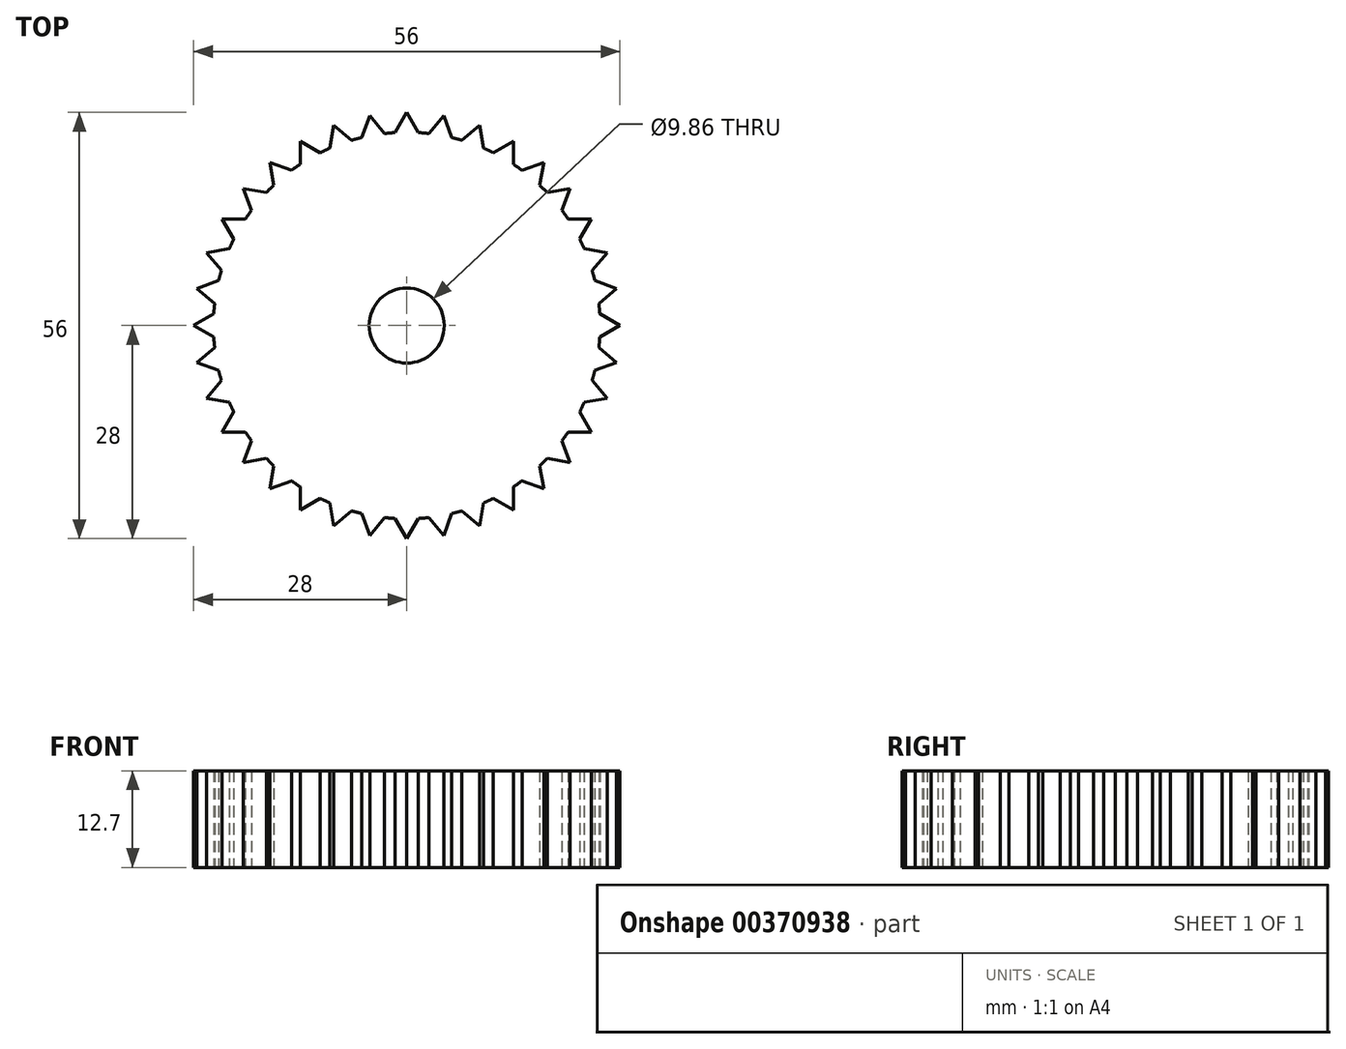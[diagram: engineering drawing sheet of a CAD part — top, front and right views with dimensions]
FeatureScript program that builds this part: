
annotation { "Feature Type Name" : "Feature", "Feature Type Description" : "" }
export const myFeature = defineFeature(function(context is Context, id is Id, definition is map)
    precondition{}
    {
        {
            var Q0;
            Q0=qCreatedBy(makeId("Top.planeOp"),FACE);
            var sketch = newSketch(context, id + "F0", { "sketchPlane" : qUnion([Q0])});
            skCircle(sketch, "E0", {"center": v(0, 0) * mm, "radius": 25.4 * mm});
            skCircle(sketch, "E1", {"center": v(0, 0) * mm, "radius": 4.93 * mm});
            skLineSegment(sketch, "E2", {"start": v(0, 28) * mm, "end": v(1.52, 25.35) * mm});
            skLineSegment(sketch, "E3", {"start": v(0, 28) * mm, "end": v(-1.52, 25.35) * mm});
            skLineSegment(sketch, "E4.1.0", {"start": v(-4.86, 27.57) * mm, "end": v(-2.9, 25.23) * mm});
            skLineSegment(sketch, "E4.1.1", {"start": v(-4.86, 27.57) * mm, "end": v(-5.9, 24.7) * mm});
            skLineSegment(sketch, "E4.2.0", {"start": v(-9.58, 26.3) * mm, "end": v(-7.24, 24.34) * mm});
            skLineSegment(sketch, "E4.2.1", {"start": v(-9.58, 26.3) * mm, "end": v(-10.1, 23.3) * mm});
            skLineSegment(sketch, "E5.3.3.0", {"start": v(-14, 24.25) * mm, "end": v(-14, 21.2) * mm});
            skLineSegment(sketch, "E5.5.3.0", {"start": v(-14, 24.25) * mm, "end": v(-11.36, 22.72) * mm});
            skLineSegment(sketch, "E5.3.4.0", {"start": v(-18, 21.45) * mm, "end": v(-17.46, 18.45) * mm});
            skLineSegment(sketch, "E5.5.4.0", {"start": v(-18, 21.45) * mm, "end": v(-15.13, 20.4) * mm});
            skLineSegment(sketch, "E5.3.5.0", {"start": v(-21.45, 18) * mm, "end": v(-20.4, 15.13) * mm});
            skLineSegment(sketch, "E5.5.5.0", {"start": v(-21.45, 18) * mm, "end": v(-18.45, 17.46) * mm});
            skLineSegment(sketch, "E6.3.6.0", {"start": v(-24.25, 14) * mm, "end": v(-22.72, 11.36) * mm});
            skLineSegment(sketch, "E6.5.6.0", {"start": v(-24.25, 14) * mm, "end": v(-21.2, 14) * mm});
            skLineSegment(sketch, "E6.3.7.0", {"start": v(-26.3, 9.58) * mm, "end": v(-24.34, 7.24) * mm});
            skLineSegment(sketch, "E6.5.7.0", {"start": v(-26.3, 9.58) * mm, "end": v(-23.3, 10.1) * mm});
            skLineSegment(sketch, "E6.3.8.0", {"start": v(-27.57, 4.86) * mm, "end": v(-25.23, 2.9) * mm});
            skLineSegment(sketch, "E6.5.8.0", {"start": v(-27.57, 4.86) * mm, "end": v(-24.7, 5.9) * mm});
            skLineSegment(sketch, "E6.3.9.0", {"start": v(-28, 0) * mm, "end": v(-25.35, -1.52) * mm});
            skLineSegment(sketch, "E6.5.9.0", {"start": v(-28, 0) * mm, "end": v(-25.35, 1.52) * mm});
            skLineSegment(sketch, "E6.3.10.0", {"start": v(-27.57, -4.86) * mm, "end": v(-24.7, -5.9) * mm});
            skLineSegment(sketch, "E6.5.10.0", {"start": v(-27.57, -4.86) * mm, "end": v(-25.23, -2.9) * mm});
            skLineSegment(sketch, "E6.3.11.0", {"start": v(-26.3, -9.58) * mm, "end": v(-23.3, -10.1) * mm});
            skLineSegment(sketch, "E6.5.11.0", {"start": v(-26.3, -9.58) * mm, "end": v(-24.34, -7.24) * mm});
            skLineSegment(sketch, "E6.3.12.0", {"start": v(-24.25, -14) * mm, "end": v(-21.2, -14) * mm});
            skLineSegment(sketch, "E6.5.12.0", {"start": v(-24.25, -14) * mm, "end": v(-22.72, -11.36) * mm});
            skLineSegment(sketch, "E6.3.13.0", {"start": v(-21.45, -18) * mm, "end": v(-18.45, -17.46) * mm});
            skLineSegment(sketch, "E6.5.13.0", {"start": v(-21.45, -18) * mm, "end": v(-20.4, -15.13) * mm});
            skLineSegment(sketch, "E6.3.14.0", {"start": v(-18, -21.45) * mm, "end": v(-15.13, -20.4) * mm});
            skLineSegment(sketch, "E6.5.14.0", {"start": v(-18, -21.45) * mm, "end": v(-17.46, -18.45) * mm});
            skLineSegment(sketch, "E6.3.15.0", {"start": v(-14, -24.25) * mm, "end": v(-11.36, -22.72) * mm});
            skLineSegment(sketch, "E6.5.15.0", {"start": v(-14, -24.25) * mm, "end": v(-14, -21.2) * mm});
            skLineSegment(sketch, "E6.3.16.0", {"start": v(-9.58, -26.3) * mm, "end": v(-7.24, -24.34) * mm});
            skLineSegment(sketch, "E6.5.16.0", {"start": v(-9.58, -26.3) * mm, "end": v(-10.1, -23.3) * mm});
            skLineSegment(sketch, "E6.3.17.0", {"start": v(-4.86, -27.57) * mm, "end": v(-2.9, -25.23) * mm});
            skLineSegment(sketch, "E6.5.17.0", {"start": v(-4.86, -27.57) * mm, "end": v(-5.9, -24.7) * mm});
            skLineSegment(sketch, "E6.3.18.0", {"start": v(0, -28) * mm, "end": v(1.52, -25.35) * mm});
            skLineSegment(sketch, "E6.5.18.0", {"start": v(0, -28) * mm, "end": v(-1.52, -25.35) * mm});
            skLineSegment(sketch, "E6.3.19.0", {"start": v(4.86, -27.57) * mm, "end": v(5.9, -24.7) * mm});
            skLineSegment(sketch, "E6.5.19.0", {"start": v(4.86, -27.57) * mm, "end": v(2.9, -25.23) * mm});
            skLineSegment(sketch, "E6.3.20.0", {"start": v(9.58, -26.3) * mm, "end": v(10.1, -23.3) * mm});
            skLineSegment(sketch, "E6.5.20.0", {"start": v(9.58, -26.3) * mm, "end": v(7.24, -24.34) * mm});
            skLineSegment(sketch, "E6.3.21.0", {"start": v(14, -24.25) * mm, "end": v(14, -21.2) * mm});
            skLineSegment(sketch, "E6.5.21.0", {"start": v(14, -24.25) * mm, "end": v(11.36, -22.72) * mm});
            skLineSegment(sketch, "E6.3.22.0", {"start": v(18, -21.45) * mm, "end": v(17.46, -18.45) * mm});
            skLineSegment(sketch, "E6.5.22.0", {"start": v(18, -21.45) * mm, "end": v(15.13, -20.4) * mm});
            skLineSegment(sketch, "E6.3.23.0", {"start": v(21.45, -18) * mm, "end": v(20.4, -15.13) * mm});
            skLineSegment(sketch, "E6.5.23.0", {"start": v(21.45, -18) * mm, "end": v(18.45, -17.46) * mm});
            skLineSegment(sketch, "E6.3.24.0", {"start": v(24.25, -14) * mm, "end": v(22.72, -11.36) * mm});
            skLineSegment(sketch, "E6.5.24.0", {"start": v(24.25, -14) * mm, "end": v(21.2, -14) * mm});
            skLineSegment(sketch, "E6.3.25.0", {"start": v(26.3, -9.58) * mm, "end": v(24.34, -7.24) * mm});
            skLineSegment(sketch, "E6.5.25.0", {"start": v(26.3, -9.58) * mm, "end": v(23.3, -10.1) * mm});
            skLineSegment(sketch, "E6.3.26.0", {"start": v(27.57, -4.86) * mm, "end": v(25.23, -2.9) * mm});
            skLineSegment(sketch, "E6.5.26.0", {"start": v(27.57, -4.86) * mm, "end": v(24.7, -5.9) * mm});
            skLineSegment(sketch, "E6.3.27.0", {"start": v(28, 0) * mm, "end": v(25.35, 1.52) * mm});
            skLineSegment(sketch, "E6.5.27.0", {"start": v(28, 0) * mm, "end": v(25.35, -1.52) * mm});
            skLineSegment(sketch, "E7.3.28.0", {"start": v(27.57, 4.86) * mm, "end": v(24.7, 5.9) * mm});
            skLineSegment(sketch, "E7.5.28.0", {"start": v(27.57, 4.86) * mm, "end": v(25.23, 2.9) * mm});
            skLineSegment(sketch, "E7.3.29.0", {"start": v(26.3, 9.58) * mm, "end": v(23.3, 10.1) * mm});
            skLineSegment(sketch, "E7.5.29.0", {"start": v(26.3, 9.58) * mm, "end": v(24.34, 7.24) * mm});
            skLineSegment(sketch, "E7.3.30.0", {"start": v(24.25, 14) * mm, "end": v(21.2, 14) * mm});
            skLineSegment(sketch, "E7.5.30.0", {"start": v(24.25, 14) * mm, "end": v(22.72, 11.36) * mm});
            skLineSegment(sketch, "E7.3.31.0", {"start": v(21.45, 18) * mm, "end": v(18.45, 17.46) * mm});
            skLineSegment(sketch, "E7.5.31.0", {"start": v(21.45, 18) * mm, "end": v(20.4, 15.13) * mm});
            skLineSegment(sketch, "E7.3.32.0", {"start": v(18, 21.45) * mm, "end": v(15.13, 20.4) * mm});
            skLineSegment(sketch, "E7.5.32.0", {"start": v(18, 21.45) * mm, "end": v(17.46, 18.45) * mm});
            skLineSegment(sketch, "E7.3.33.0", {"start": v(14, 24.25) * mm, "end": v(11.36, 22.72) * mm});
            skLineSegment(sketch, "E7.5.33.0", {"start": v(14, 24.25) * mm, "end": v(14, 21.2) * mm});
            skLineSegment(sketch, "E7.3.34.0", {"start": v(9.58, 26.3) * mm, "end": v(7.24, 24.34) * mm});
            skLineSegment(sketch, "E7.5.34.0", {"start": v(9.58, 26.3) * mm, "end": v(10.1, 23.3) * mm});
            skLineSegment(sketch, "E7.3.35.0", {"start": v(4.86, 27.57) * mm, "end": v(2.9, 25.23) * mm});
            skLineSegment(sketch, "E7.5.35.0", {"start": v(4.86, 27.57) * mm, "end": v(5.9, 24.7) * mm});
            skSolve(sketch);
        }
        {
            var Q0;
            Q0 = qSketchRegion(id + "F0", true);
            var Q1;
            {var subQ0=sQuery(id+"F0.wireOp",EDGE,"E6.3.14.0");Q1=makeQuery(id+"F0.imprint","IMPRINT",FACE,{"disambiguationData":[TD([[makeQuery(id+"F0.imprint","IMPRINT",EDGE,{"derivedFrom":subQ0}),1.0]])]});}
            var Q2;
            {var subQ0=sQuery(id+"F0.wireOp",EDGE,"E6.3.17.0");Q2=makeQuery(id+"F0.imprint","IMPRINT",FACE,{"disambiguationData":[TD([[makeQuery(id+"F0.imprint","IMPRINT",EDGE,{"derivedFrom":subQ0}),1.0]])]});}
            var Q3;
            {var subQ0=sQuery(id+"F0.wireOp",EDGE,"E6.3.26.0");Q3=makeQuery(id+"F0.imprint","IMPRINT",FACE,{"disambiguationData":[TD([[makeQuery(id+"F0.imprint","IMPRINT",EDGE,{"derivedFrom":subQ0}),1.0]])]});}
            var Q4;
            {var subQ0=sQuery(id+"F0.wireOp",EDGE,"E6.3.25.0");Q4=makeQuery(id+"F0.imprint","IMPRINT",FACE,{"disambiguationData":[TD([[makeQuery(id+"F0.imprint","IMPRINT",EDGE,{"derivedFrom":subQ0}),1.0]])]});}
            var Q5;
            {var subQ0=sQuery(id+"F0.wireOp",EDGE,"E4.2.0");Q5=makeQuery(id+"F0.imprint","IMPRINT",FACE,{"disambiguationData":[TD([[makeQuery(id+"F0.imprint","IMPRINT",EDGE,{"derivedFrom":subQ0}),-1.0]])]});}
            var Q6;
            {var subQ0=sQuery(id+"F0.wireOp",EDGE,"E4.1.0");Q6=makeQuery(id+"F0.imprint","IMPRINT",FACE,{"disambiguationData":[TD([[makeQuery(id+"F0.imprint","IMPRINT",EDGE,{"derivedFrom":subQ0}),-1.0]])]});}
            var Q7;
            {var subQ0=sQuery(id+"F0.wireOp",EDGE,"E7.3.34.0");Q7=makeQuery(id+"F0.imprint","IMPRINT",FACE,{"disambiguationData":[TD([[makeQuery(id+"F0.imprint","IMPRINT",EDGE,{"derivedFrom":subQ0}),1.0]])]});}
            var Q8;
            {var subQ0=sQuery(id+"F0.wireOp",EDGE,"E7.3.29.0");Q8=makeQuery(id+"F0.imprint","IMPRINT",FACE,{"disambiguationData":[TD([[makeQuery(id+"F0.imprint","IMPRINT",EDGE,{"derivedFrom":subQ0}),1.0]])]});}
            var Q9;
            {var subQ0=sQuery(id+"F0.wireOp",EDGE,"E6.3.8.0");Q9=makeQuery(id+"F0.imprint","IMPRINT",FACE,{"disambiguationData":[TD([[makeQuery(id+"F0.imprint","IMPRINT",EDGE,{"derivedFrom":subQ0}),1.0]])]});}
            var Q10;
            {var subQ0=sQuery(id+"F0.wireOp",EDGE,"E5.3.5.0");Q10=makeQuery(id+"F0.imprint","IMPRINT",FACE,{"disambiguationData":[TD([[makeQuery(id+"F0.imprint","IMPRINT",EDGE,{"derivedFrom":subQ0}),1.0]])]});}
            var Q11;
            {var subQ0=sQuery(id+"F0.wireOp",EDGE,"E6.3.18.0");Q11=makeQuery(id+"F0.imprint","IMPRINT",FACE,{"disambiguationData":[TD([[makeQuery(id+"F0.imprint","IMPRINT",EDGE,{"derivedFrom":subQ0}),1.0]])]});}
            var Q12;
            {var subQ0=sQuery(id+"F0.wireOp",EDGE,"E6.3.10.0");Q12=makeQuery(id+"F0.imprint","IMPRINT",FACE,{"disambiguationData":[TD([[makeQuery(id+"F0.imprint","IMPRINT",EDGE,{"derivedFrom":subQ0}),1.0]])]});}
            var Q13;
            {var subQ0=sQuery(id+"F0.wireOp",EDGE,"E5.3.4.0");Q13=makeQuery(id+"F0.imprint","IMPRINT",FACE,{"disambiguationData":[TD([[makeQuery(id+"F0.imprint","IMPRINT",EDGE,{"derivedFrom":subQ0}),1.0]])]});}
            var Q14;
            {var subQ0=sQuery(id+"F0.wireOp",EDGE,"E2");Q14=makeQuery(id+"F0.imprint","IMPRINT",FACE,{"disambiguationData":[TD([[makeQuery(id+"F0.imprint","IMPRINT",EDGE,{"derivedFrom":subQ0}),-1.0]])]});}
            var Q15;
            {var subQ0=sQuery(id+"F0.wireOp",EDGE,"E7.3.30.0");Q15=makeQuery(id+"F0.imprint","IMPRINT",FACE,{"disambiguationData":[TD([[makeQuery(id+"F0.imprint","IMPRINT",EDGE,{"derivedFrom":subQ0}),1.0]])]});}
            var Q16;
            {var subQ0=sQuery(id+"F0.wireOp",EDGE,"E7.3.28.0");Q16=makeQuery(id+"F0.imprint","IMPRINT",FACE,{"disambiguationData":[TD([[makeQuery(id+"F0.imprint","IMPRINT",EDGE,{"derivedFrom":subQ0}),1.0]])]});}
            var Q17;
            {var subQ0=sQuery(id+"F0.wireOp",EDGE,"E6.3.24.0");Q17=makeQuery(id+"F0.imprint","IMPRINT",FACE,{"disambiguationData":[TD([[makeQuery(id+"F0.imprint","IMPRINT",EDGE,{"derivedFrom":subQ0}),1.0]])]});}
            var Q18;
            {var subQ0=sQuery(id+"F0.wireOp",EDGE,"E6.3.6.0");Q18=makeQuery(id+"F0.imprint","IMPRINT",FACE,{"disambiguationData":[TD([[makeQuery(id+"F0.imprint","IMPRINT",EDGE,{"derivedFrom":subQ0}),1.0]])]});}
            var Q19;
            Q19=makeQuery(id+"F0.imprint","IMPRINT",FACE,{"disambiguationData":[TD([[makeQuery(id+"F0.imprint","IMPRINT",EDGE,{"derivedFrom":sQuery(id+"F0.wireOp",EDGE,"E1")}),-1.0]])]});
            var Q20;
            {var subQ0=sQuery(id+"F0.wireOp",EDGE,"E6.3.13.0");Q20=makeQuery(id+"F0.imprint","IMPRINT",FACE,{"disambiguationData":[TD([[makeQuery(id+"F0.imprint","IMPRINT",EDGE,{"derivedFrom":subQ0}),1.0]])]});}
            var Q21;
            {var subQ0=sQuery(id+"F0.wireOp",EDGE,"E6.3.12.0");Q21=makeQuery(id+"F0.imprint","IMPRINT",FACE,{"disambiguationData":[TD([[makeQuery(id+"F0.imprint","IMPRINT",EDGE,{"derivedFrom":subQ0}),1.0]])]});}
            var Q22;
            {var subQ0=sQuery(id+"F0.wireOp",EDGE,"E5.3.3.0");Q22=makeQuery(id+"F0.imprint","IMPRINT",FACE,{"disambiguationData":[TD([[makeQuery(id+"F0.imprint","IMPRINT",EDGE,{"derivedFrom":subQ0}),1.0]])]});}
            var Q23;
            {var subQ0=sQuery(id+"F0.wireOp",EDGE,"E7.3.32.0");Q23=makeQuery(id+"F0.imprint","IMPRINT",FACE,{"disambiguationData":[TD([[makeQuery(id+"F0.imprint","IMPRINT",EDGE,{"derivedFrom":subQ0}),1.0]])]});}
            var Q24;
            {var subQ0=sQuery(id+"F0.wireOp",EDGE,"E6.3.22.0");Q24=makeQuery(id+"F0.imprint","IMPRINT",FACE,{"disambiguationData":[TD([[makeQuery(id+"F0.imprint","IMPRINT",EDGE,{"derivedFrom":subQ0}),1.0]])]});}
            var Q25;
            {var subQ0=sQuery(id+"F0.wireOp",EDGE,"E6.3.19.0");Q25=makeQuery(id+"F0.imprint","IMPRINT",FACE,{"disambiguationData":[TD([[makeQuery(id+"F0.imprint","IMPRINT",EDGE,{"derivedFrom":subQ0}),1.0]])]});}
            var Q26;
            {var subQ0=sQuery(id+"F0.wireOp",EDGE,"E6.3.27.0");Q26=makeQuery(id+"F0.imprint","IMPRINT",FACE,{"disambiguationData":[TD([[makeQuery(id+"F0.imprint","IMPRINT",EDGE,{"derivedFrom":subQ0}),1.0]])]});}
            var Q27;
            {var subQ0=sQuery(id+"F0.wireOp",EDGE,"E6.3.11.0");Q27=makeQuery(id+"F0.imprint","IMPRINT",FACE,{"disambiguationData":[TD([[makeQuery(id+"F0.imprint","IMPRINT",EDGE,{"derivedFrom":subQ0}),1.0]])]});}
            var Q28;
            {var subQ0=sQuery(id+"F0.wireOp",EDGE,"E6.3.23.0");Q28=makeQuery(id+"F0.imprint","IMPRINT",FACE,{"disambiguationData":[TD([[makeQuery(id+"F0.imprint","IMPRINT",EDGE,{"derivedFrom":subQ0}),1.0]])]});}
            var Q29;
            {var subQ0=sQuery(id+"F0.wireOp",EDGE,"E6.3.16.0");Q29=makeQuery(id+"F0.imprint","IMPRINT",FACE,{"disambiguationData":[TD([[makeQuery(id+"F0.imprint","IMPRINT",EDGE,{"derivedFrom":subQ0}),1.0]])]});}
            var Q30;
            {var subQ0=sQuery(id+"F0.wireOp",EDGE,"E6.3.9.0");Q30=makeQuery(id+"F0.imprint","IMPRINT",FACE,{"disambiguationData":[TD([[makeQuery(id+"F0.imprint","IMPRINT",EDGE,{"derivedFrom":subQ0}),1.0]])]});}
            var Q31;
            {var subQ0=sQuery(id+"F0.wireOp",EDGE,"E6.3.15.0");Q31=makeQuery(id+"F0.imprint","IMPRINT",FACE,{"disambiguationData":[TD([[makeQuery(id+"F0.imprint","IMPRINT",EDGE,{"derivedFrom":subQ0}),1.0]])]});}
            var Q32;
            {var subQ0=sQuery(id+"F0.wireOp",EDGE,"E7.3.35.0");Q32=makeQuery(id+"F0.imprint","IMPRINT",FACE,{"disambiguationData":[TD([[makeQuery(id+"F0.imprint","IMPRINT",EDGE,{"derivedFrom":subQ0}),1.0]])]});}
            var Q33;
            {var subQ0=sQuery(id+"F0.wireOp",EDGE,"E7.3.33.0");Q33=makeQuery(id+"F0.imprint","IMPRINT",FACE,{"disambiguationData":[TD([[makeQuery(id+"F0.imprint","IMPRINT",EDGE,{"derivedFrom":subQ0}),1.0]])]});}
            var Q34;
            {var subQ0=sQuery(id+"F0.wireOp",EDGE,"E7.3.31.0");Q34=makeQuery(id+"F0.imprint","IMPRINT",FACE,{"disambiguationData":[TD([[makeQuery(id+"F0.imprint","IMPRINT",EDGE,{"derivedFrom":subQ0}),1.0]])]});}
            var Q35;
            {var subQ0=sQuery(id+"F0.wireOp",EDGE,"E6.3.7.0");Q35=makeQuery(id+"F0.imprint","IMPRINT",FACE,{"disambiguationData":[TD([[makeQuery(id+"F0.imprint","IMPRINT",EDGE,{"derivedFrom":subQ0}),1.0]])]});}
            var Q36;
            {var subQ0=sQuery(id+"F0.wireOp",EDGE,"E6.3.20.0");Q36=makeQuery(id+"F0.imprint","IMPRINT",FACE,{"disambiguationData":[TD([[makeQuery(id+"F0.imprint","IMPRINT",EDGE,{"derivedFrom":subQ0}),1.0]])]});}
            var Q37;
            {var subQ0=sQuery(id+"F0.wireOp",EDGE,"E6.3.21.0");Q37=makeQuery(id+"F0.imprint","IMPRINT",FACE,{"disambiguationData":[TD([[makeQuery(id+"F0.imprint","IMPRINT",EDGE,{"derivedFrom":subQ0}),1.0]])]});}
            extrude(context, id + "F1", {"entities" : qUnion([Q0, Q1, Q2, Q3, Q4, Q5, Q6, Q7, Q8, Q9, Q10, Q11, Q12, Q13, Q14, Q15, Q16, Q17, Q18, Q19, Q20, Q21, Q22, Q23, Q24, Q25, Q26, Q27, Q28, Q29, Q30, Q31, Q32, Q33, Q34, Q35, Q36, Q37]), "depth" : 12.7 * mm});
        }
    });
